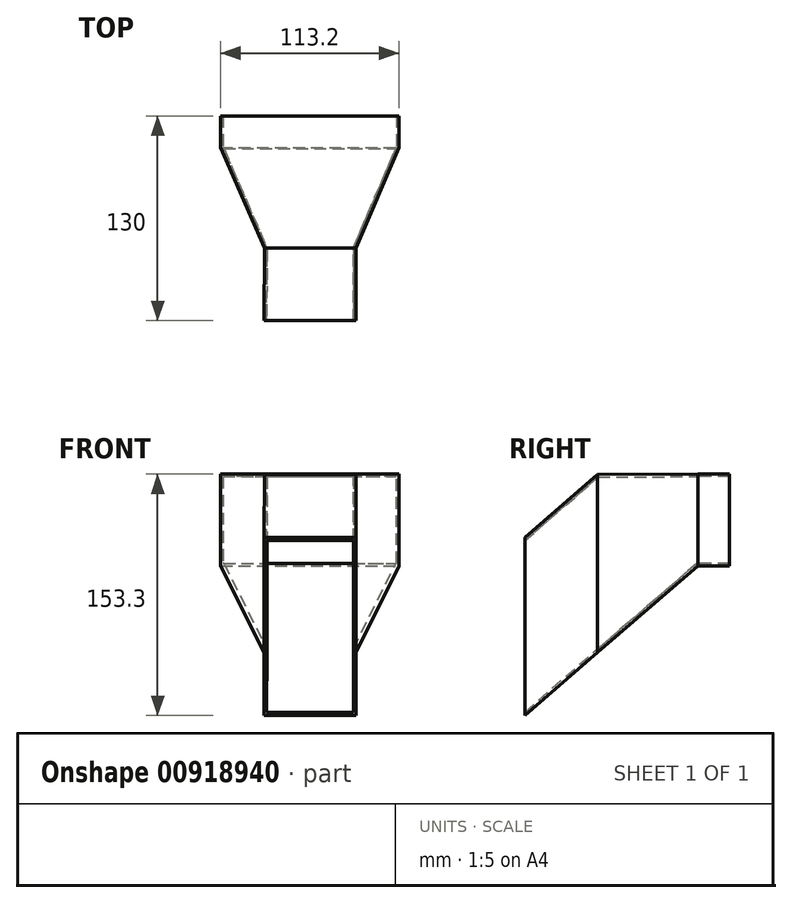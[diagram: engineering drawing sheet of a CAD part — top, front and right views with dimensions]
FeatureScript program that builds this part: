
annotation { "Feature Type Name" : "Feature", "Feature Type Description" : "" }
export const myFeature = defineFeature(function(context is Context, id is Id, definition is map)
    precondition{}
    {
        {
            var Q0;
            Q0=qCreatedBy(makeId("Front.planeOp"),FACE);
            var sketch = newSketch(context, id + "F0", { "sketchPlane" : qUnion([Q0])});
            skLineSegment(sketch, "E0.bottom", {"start": v(-56.45, 58.3) * mm, "end": v(56.75, 58.3) * mm});
            skLineSegment(sketch, "E0.top", {"start": v(-56.45, 0.1) * mm, "end": v(56.75, 0.1) * mm});
            skLineSegment(sketch, "E0.left", {"start": v(-56.45, 58.3) * mm, "end": v(-56.45, 0.1) * mm});
            skLineSegment(sketch, "E0.right", {"start": v(56.75, 58.3) * mm, "end": v(56.75, 0.1) * mm});
            skSolve(sketch);
        }
        {
            var Q0;
            Q0=qCreatedBy(makeId("Front.planeOp"),FACE);
            var Q1;
            Q1=qBodyType(qCreatedBy(id+"F2",EDGE),BodyType.WIRE);
            cPlane(context, id + "F1", {"entities" : qUnion([Q0, Q1]), "cplaneType" : CPlaneType.OFFSET, "offset" : 64 * mm, "width" : 150 * mm, "height" : 150 * mm});
        }
        {
            var Q0;
            Q0=qCreatedBy(id+"F1.planeOp",FACE);
            var sketch = newSketch(context, id + "F2", { "sketchPlane" : qUnion([Q0])});
            skLineSegment(sketch, "E1.bottom", {"start": v(-28.73, 58.2) * mm, "end": v(29.47, 58.2) * mm});
            skLineSegment(sketch, "E1.top", {"start": v(-28.73, -55) * mm, "end": v(29.47, -55) * mm});
            skLineSegment(sketch, "E1.left", {"start": v(-28.73, 58.2) * mm, "end": v(-28.73, -55) * mm});
            skLineSegment(sketch, "E1.right", {"start": v(29.47, 58.2) * mm, "end": v(29.47, -55) * mm});
            skSolve(sketch);
        }
        {
            var Q0;
            Q0=makeQuery(id+"F0.imprint","IMPRINT",FACE,{"disambiguationData":[TD([[makeQuery(id+"F0.imprint","IMPRINT",EDGE,{"derivedFrom":sQuery(id+"F0.wireOp",EDGE,"E0.bottom")}),-1.0]])]});
            var Q1;
            Q1=makeQuery(id+"F2.imprint","IMPRINT",FACE,{"disambiguationData":[TD([[makeQuery(id+"F2.imprint","IMPRINT",EDGE,{"derivedFrom":sQuery(id+"F2.wireOp",EDGE,"E1.bottom")}),-1.0]])]});
            loft(context, id + "F3", {"sheetProfilesArray" : [{ "sheetProfileEntities" : qUnion([Q0]) }, { "sheetProfileEntities" : qUnion([Q1]) }]});
        }
        {
            var Q0;
            Q0=makeQuery(id+"F3.opLoft","CAP_FACE",FACE,{"disambiguationData":[OSD([makeQuery(id+"F0.imprint","IMPRINT",FACE,{"disambiguationData":[TD([[makeQuery(id+"F0.imprint","IMPRINT",EDGE,{"derivedFrom":sQuery(id+"F0.wireOp",EDGE,"E0.bottom")}),-1.0]])]})])],"isStart":true});
            extrude(context, id + "F4", {"entities" : qUnion([Q0]), "operationType" : NewBodyOperationType.ADD, "depth" : 20 * mm, "offsetDistance" : 25 * mm});
        }
        {
            var Q0;
            Q0=qCreatedBy(makeId("Front.planeOp"),FACE);
            cPlane(context, id + "F5", {"entities" : qUnion([Q0]), "cplaneType" : CPlaneType.OFFSET, "offset" : 110 * mm, "width" : 150 * mm, "height" : 150 * mm});
        }
        {
            var Q0;
            Q0=qCreatedBy(id+"F5.planeOp",FACE);
            var sketch = newSketch(context, id + "F6", { "sketchPlane" : qUnion([Q0])});
            skLineSegment(sketch, "E2.bottom", {"start": v(-28.78, 18.2) * mm, "end": v(29.42, 18.2) * mm});
            skLineSegment(sketch, "E2.top", {"start": v(-28.78, -95) * mm, "end": v(29.42, -95) * mm});
            skLineSegment(sketch, "E2.left", {"start": v(-28.78, 18.2) * mm, "end": v(-28.78, -95) * mm});
            skLineSegment(sketch, "E2.right", {"start": v(29.42, 18.2) * mm, "end": v(29.42, -95) * mm});
            skSolve(sketch);
        }
        {
            var Q1;
            Q1=makeQuery(id+"F2.imprint","IMPRINT",FACE,{"disambiguationData":[TD([[makeQuery(id+"F2.imprint","IMPRINT",EDGE,{"derivedFrom":sQuery(id+"F2.wireOp",EDGE,"E1.bottom")}),-1.0]])]});
            var Q2;
            Q2=makeQuery(id+"F6.imprint","IMPRINT",FACE,{"disambiguationData":[TD([[makeQuery(id+"F6.imprint","IMPRINT",EDGE,{"derivedFrom":sQuery(id+"F6.wireOp",EDGE,"E2.bottom")}),-1.0]])]});
            loft(context, id + "F7", {"operationType" : NewBodyOperationType.ADD, "sheetProfilesArray" : [{ "sheetProfileEntities" : qUnion([Q1]) }, { "sheetProfileEntities" : qUnion([Q2]) }]});
        }
        {
            var Q0;
            Q0=makeQuery(id+"F4.opExtrude","CAP_FACE",FACE,{"disambiguationData":[OSD([makeQuery(id+"F0.imprint","IMPRINT",FACE,{"disambiguationData":[TD([[makeQuery(id+"F0.imprint","IMPRINT",EDGE,{"derivedFrom":sQuery(id+"F0.wireOp",EDGE,"E0.bottom")}),-1.0]])]})])],"isStart":false});
            var Q1;
            Q1=makeQuery(id+"F7.opLoft","CAP_FACE",FACE,{"disambiguationData":[OSD([makeQuery(id+"F6.imprint","IMPRINT",FACE,{"disambiguationData":[TD([[makeQuery(id+"F6.imprint","IMPRINT",EDGE,{"derivedFrom":sQuery(id+"F6.wireOp",EDGE,"E2.bottom")}),-1.0]])]})])],"isStart":true});
            shell(context, id + "F8", {"entities" : qUnion([Q0, Q1]), "thickness" : 1.6 * mm});
        }
    });
